# Revit family: 4LRS4834B5T,B2T,B5B,B2B
name_source: partatom
category: Plumbing Fixtures
revit_build: Autodesk Revit LT 2014 (Build: 20130308_1515(x64)
units: mm (PartAtom-declared; Revit-internal decimal feet)

## types (4) — shared parameters
Assembly Code = D2010710
Keynote = 22 40 00.B3
Manufacturer = Best Bath Systems, Inc.
Type Comments = Barrier Free
URL = http://www.best-bath.com
Unit Width = 4' - 0"

## per-type parameters (varying)
| type | Description | Threshold Height | Unit Height |
| 4LRS4834B5B | Real Tile, Beveled Threshold | 0' - 0 5/8" | 6' - 9 1/8" |
| 4LRS4834B2B | Real Tile, Beveled Threshold | 0' - 2" | 6' - 10 1/2" |
| 4LRS4834B5T | Real Tile, Traditional Bull Nose Threshold | 0' - 0 5/8" | 6' - 9 1/8" |
| 4LRS4834B2T | Real Tile, Traditional Bull Nose Threshold | 0' - 2" | 6' - 10 1/2" |

note: column(s) folded — value = type name in every type: Model

## geometry (parser evidence)
native form markers: Blend x22, Sweep x1
no freeform markers — native parametric forms only
